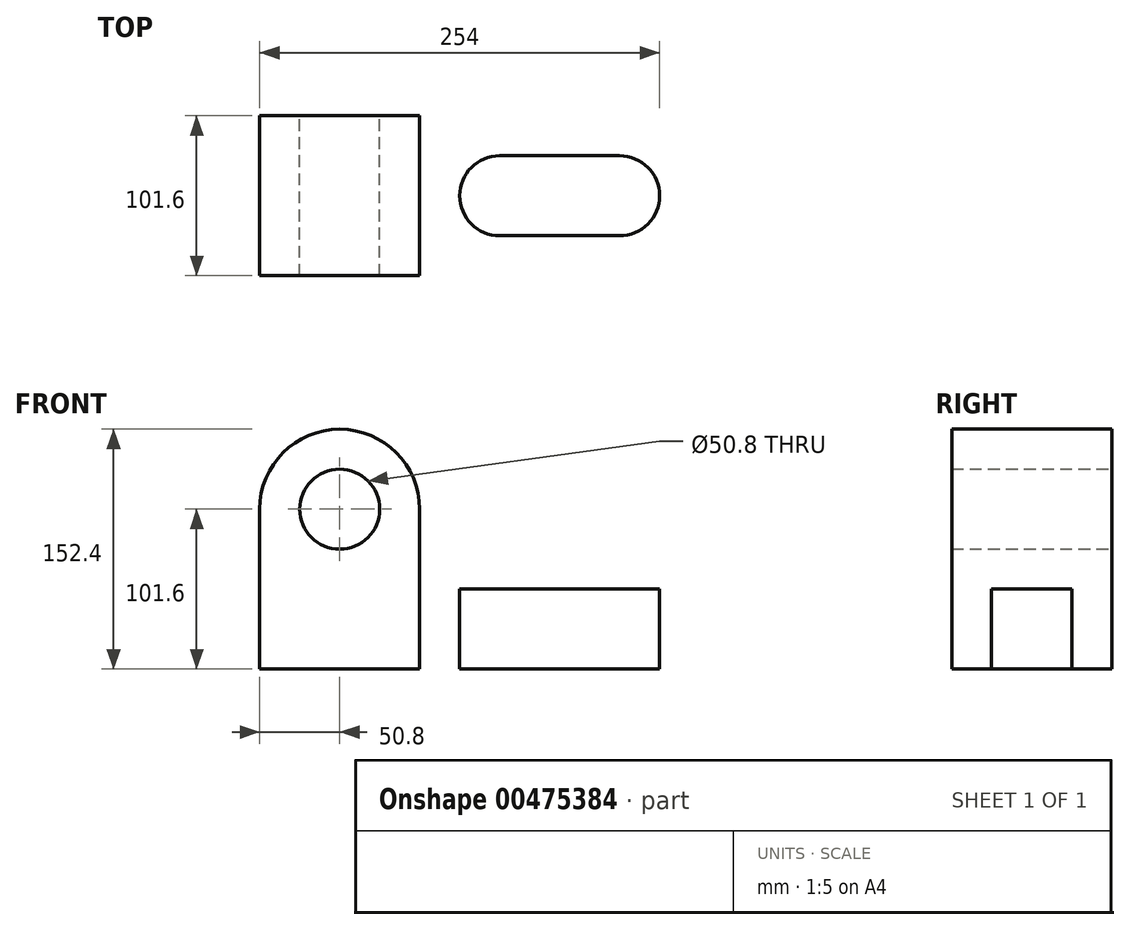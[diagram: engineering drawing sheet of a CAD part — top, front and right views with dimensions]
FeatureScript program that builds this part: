
annotation { "Feature Type Name" : "Feature", "Feature Type Description" : "" }
export const myFeature = defineFeature(function(context is Context, id is Id, definition is map)
    precondition{}
    {
        {
            var Q0;
            Q0=qCreatedBy(makeId("Front.planeOp"),FACE);
            var sketch = newSketch(context, id + "F0", { "sketchPlane" : qUnion([Q0])});
            skLineSegment(sketch, "E0.bottom", {"start": v(0, 0) * mm, "end": v(279.4, 0) * mm});
            skLineSegment(sketch, "E0.top", {"start": v(0, 152.4) * mm, "end": v(279.4, 152.4) * mm});
            skLineSegment(sketch, "E0.left", {"start": v(0, 0) * mm, "end": v(0, 152.4) * mm});
            skLineSegment(sketch, "E0.right", {"start": v(279.4, 0) * mm, "end": v(279.4, 152.4) * mm});
            skCircle(sketch, "E1", {"center": v(50.8, 101.6) * mm, "radius": 50.8 * mm});
            skCircle(sketch, "E2", {"center": v(50.8, 101.6) * mm, "radius": 25.4 * mm});
            skLineSegment(sketch, "E3", {"start": v(101.6, 101.6) * mm, "end": v(101.6, 50.8) * mm});
            skLineSegment(sketch, "E4", {"start": v(101.6, 50.8) * mm, "end": v(279.4, 50.8) * mm});
            skSolve(sketch);
        }
        {
            var Q0;
            Q0=makeQuery(id+"F0.imprint","IMPRINT",FACE,{"disambiguationData":[TD([[makeQuery(id+"F0.imprint","IMPRINT",EDGE,{"derivedFrom":sQuery(id+"F0.wireOp",EDGE,"E2")}),-1.0]])]});
            var Q1;
            {var subQ4=sQuery(id+"F0.wireOp",EDGE,"E0.bottom");Q1=makeQuery(id+"F0.imprint","IMPRINT",FACE,{"disambiguationData":[TD([[makeQuery(id+"F0.imprint","IMPRINT",EDGE,{"derivedFrom":subQ4}),1.0]])]});}
            extrude(context, id + "F1", {"entities" : qUnion([Q0, Q1]), "depth" : 101.6 * mm, "offsetDistance" : 25.4 * mm});
        }
        {
            var Q0;
            Q0=makeQuery(id+"F1.opExtrude","SWEPT_FACE",FACE,{"disambiguationData":[OSD([sQuery(id+"F0.wireOp",EDGE,"E4")])]});
            var sketch = newSketch(context, id + "F2", { "sketchPlane" : qUnion([Q0])});
            skCircle(sketch, "E5", {"center": v(228.6, -50.8) * mm, "radius": 50.8 * mm});
            skLineSegment(sketch, "E6", {"start": v(228.6, -50.8) * mm, "end": v(152.4, -50.8) * mm});
            skArc(sketch, "E7.0.startCap", {"start": v(228.6, -25.4) * mm, "mid": v(254, -50.8) * mm, "end": v(228.6, -76.2) * mm});
            skArc(sketch, "E7.0.endCap", {"start": v(152.4, -76.2) * mm, "mid": v(127, -50.8) * mm, "end": v(152.4, -25.4) * mm});
            skLineSegment(sketch, "E7.0.left", {"start": v(228.6, -76.2) * mm, "end": v(152.4, -76.2) * mm});
            skLineSegment(sketch, "E7.0.right", {"start": v(228.6, -25.4) * mm, "end": v(152.4, -25.4) * mm});
            skSolve(sketch);
        }
        {
            var Q0;
            {var subQ0=sQuery(id+"F2.wireOp",EDGE,"E7.0.startCap");Q0=makeQuery(id+"F2.imprint","IMPRINT",FACE,{"disambiguationData":[TD([[makeQuery(id+"F2.imprint","IMPRINT",EDGE,{"derivedFrom":subQ0}),-1.0]])]});}
            var Q1;
            {var subQ1=sQuery(id+"F2.wireOp",EDGE,"E7.0.endCap");Q1=makeQuery(id+"F2.imprint","IMPRINT",FACE,{"disambiguationData":[TD([[makeQuery(id+"F2.imprint","IMPRINT",EDGE,{"derivedFrom":subQ1}),-1.0]])]});}
            var Q2;
            {var subQ0=sQuery(id+"F2.wireOp",EDGE,"E5");var subQ1=sQuery(id+"F0.wireOp",EDGE,"E4");var subQ2=makeQuery(id+"F1.opExtrude","CAP_EDGE",EDGE,{"disambiguationData":[OSD([subQ1])],"isStart":true});var subQ3=makeQuery(id+"F2.imprint","INTERSECT",VERTEX,{"derivedFrom":[subQ2,subQ0]});Q2=makeQuery(id+"F2.imprint","IMPRINT",FACE,{"disambiguationData":[TD([[makeQuery(id+"F2.imprint","IMPRINT",EDGE,{"disambiguationData":[TD([[subQ3,1.0]])],"derivedFrom":subQ0}),-1.0]])]});}
            var Q3;
            {var subQ0=sQuery(id+"F2.wireOp",EDGE,"E5");var subQ1=sQuery(id+"F0.wireOp",EDGE,"E4");var subQ4=makeQuery(id+"F1.opExtrude","CAP_EDGE",EDGE,{"disambiguationData":[OSD([subQ1])],"isStart":false});var subQ5=makeQuery(id+"F2.imprint","INTERSECT",VERTEX,{"derivedFrom":[subQ4,subQ0]});Q3=makeQuery(id+"F2.imprint","IMPRINT",FACE,{"disambiguationData":[TD([[makeQuery(id+"F2.imprint","IMPRINT",EDGE,{"disambiguationData":[TD([[subQ5,-1.0]])],"derivedFrom":subQ0}),-1.0]])]});}
            extrude(context, id + "F3", {"entities" : qUnion([Q0, Q1, Q2, Q3]), "operationType" : NewBodyOperationType.REMOVE, "endBound" : BoundingType.THROUGH_ALL, "oppositeDirection" : true, "depth" : 25.4 * mm, "offsetDistance" : 25.4 * mm});
        }
    });
